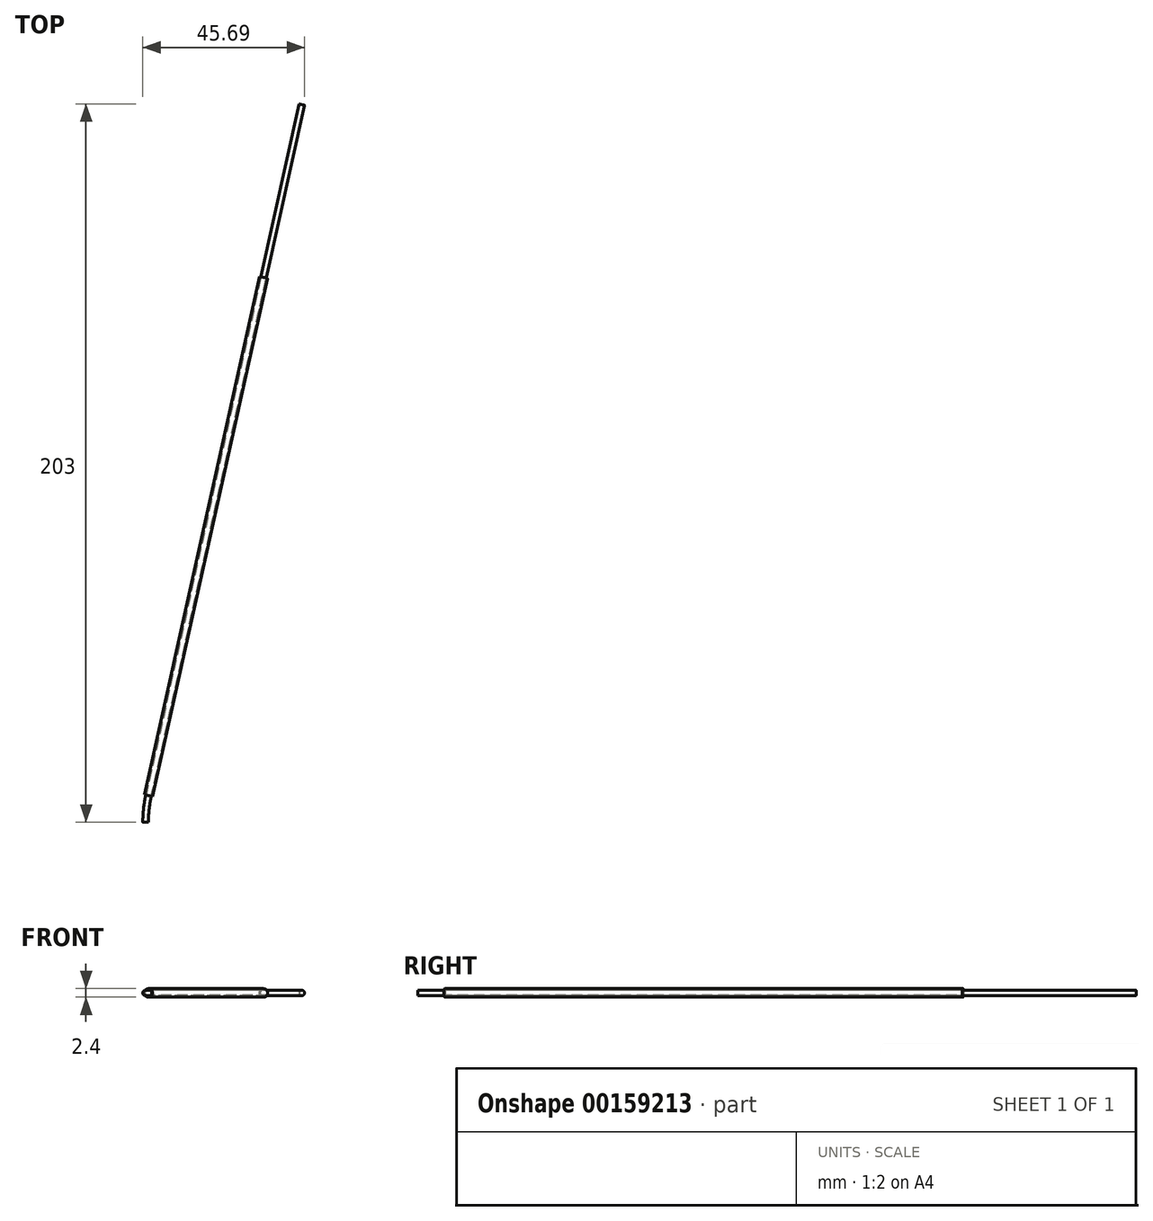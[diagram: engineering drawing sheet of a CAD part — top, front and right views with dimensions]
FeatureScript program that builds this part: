
annotation { "Feature Type Name" : "Feature", "Feature Type Description" : "" }
export const myFeature = defineFeature(function(context is Context, id is Id, definition is map)
    precondition{}
    {
        {
            assignVariable(context, id + "F0", {"name" : "TubeTransmissionLength", "anyValue" : 200});
        }
        {
            assignVariable(context, id + "F1", {"name" : "Angle", "anyValue" : 12.5});
        }
        {
            var Q0;
            Q0=qCreatedBy(makeId("Front.planeOp"),FACE);
            var sketch = newSketch(context, id + "F2", { "sketchPlane" : qUnion([Q0])});
            skCircle(sketch, "E0", {"center": v(0, 0) * mm, "radius": 0.7 * mm});
            skCircle(sketch, "E1", {"center": v(0, 0) * mm, "radius": 0.8 * mm});
            skSolve(sketch);
        }
        {
            var Q0;
            Q0=qCreatedBy(makeId("Top.planeOp"),FACE);
            var sketch = newSketch(context, id + "F3", { "sketchPlane" : qUnion([Q0])});
            skLineSegment(sketch, "E2", {"start": v(0, 0) * mm, "end": v(0, -200) * mm});
            skLineSegment(sketch, "E3", {"start": v(0, -145.32) * mm, "end": v(0, -200) * mm, "construction": true});
            skLineSegment(sketch, "E4", {"start": v(0, -200) * mm, "end": v(-35, -200) * mm, "construction": true});
            skArc(sketch, "E5", {"start": v(0, -200) * mm, "mid": v(-0.2, -203.8) * mm, "end": v(-0.83, -207.57) * mm});
            skSolve(sketch);
        }
        {
            var Q0;
            Q0=makeQuery(id+"F2.imprint","IMPRINT",FACE,{"disambiguationData":[TD([[makeQuery(id+"F2.imprint","IMPRINT",EDGE,{"derivedFrom":sQuery(id+"F2.wireOp",EDGE,"E0")}),-1.0]])]});
            var Q1;
            Q1=sQuery(id+"F3.wireOp",EDGE,"E2");
            var Q2;
            Q2=sQuery(id+"F3.wireOp",EDGE,"E5");
            sweep(context, id + "F4", {"profiles" : qUnion([Q0]), "path" : qUnion([Q1, Q2])});
        }
        {
            var Q0;
            Q0=makeQuery(id+"F4.opSweep","CAP_FACE",FACE,{"disambiguationData":[OSD([sQuery(id+"F2.wireOp",EDGE,"E0"),sQuery(id+"F2.wireOp",EDGE,"E1"),sQuery(id+"F3.wireOp",VERTEX,"E2.start")])],"isStart":true});
            cPlane(context, id + "F5", {"entities" : qUnion([Q0]), "cplaneType" : CPlaneType.OFFSET, "offset" : 50 * mm, "oppositeDirection" : true, "width" : 150 * mm, "height" : 150 * mm});
        }
        {
            var Q0;
            Q0=qCreatedBy(id+"F5.planeOp",FACE);
            var sketch = newSketch(context, id + "F6", { "sketchPlane" : qUnion([Q0])});
            skCircle(sketch, "E6.0", {"center": v(0, 0) * mm, "radius": 0.8 * mm});
            skCircle(sketch, "E6.1", {"center": v(0, 0) * mm, "radius": 0.7 * mm});
            skCircle(sketch, "E7", {"center": v(0, 0) * mm, "radius": 0.9 * mm});
            skCircle(sketch, "E8", {"center": v(0, 0) * mm, "radius": 1.2 * mm});
            skSolve(sketch);
        }
        {
            var Q0;
            Q0=makeQuery(id+"F6.imprint","IMPRINT",FACE,{"disambiguationData":[TD([[makeQuery(id+"F6.imprint","IMPRINT",EDGE,{"derivedFrom":sQuery(id+"F6.wireOp",EDGE,"E7")}),-1.0]])]});
            var Q1;
            Q1=makeQuery(id+"F4.opSweep","SWEPT_FACE",FACE,{"disambiguationData":[OSD([sQuery(id+"F2.wireOp",EDGE,"E1"),sQuery(id+"F3.wireOp",EDGE,"E2")])]});
            extrude(context, id + "F7", {"entities" : qUnion([Q0]), "oppositeDirection" : true, "endBoundEntityFace" : qUnion([Q1]), "depth" : (getVariable(context, 'TubeTransmissionLength') - 50) * mm});
        }
        {
            var Q0;
            Q0=makeQuery(id+"F7.opExtrude","CAP_FACE",FACE,{"disambiguationData":[OSD([sQuery(id+"F6.wireOp",EDGE,"E7"),sQuery(id+"F6.wireOp",EDGE,"E8")])],"isStart":true});
            cPlane(context, id + "F8", {"entities" : qUnion([Q0]), "cplaneType" : CPlaneType.OFFSET, "offset" : 50 * mm, "oppositeDirection" : true, "width" : 150 * mm, "height" : 150 * mm});
        }
        {
            var Q0;
            Q0=qCreatedBy(id+"F8.planeOp",FACE);
            var sketch = newSketch(context, id + "F9", { "sketchPlane" : qUnion([Q0])});
            skCircle(sketch, "E9.0", {"center": v(0, 0) * mm, "radius": 1.2 * mm});
            skLineSegment(sketch, "E10", {"start": v(0, 0) * mm, "end": v(0, 9.07) * mm});
            skLineSegment(sketch, "E11", {"start": v(0, 0) * mm, "end": v(-8.67, 0) * mm});
            skSolve(sketch);
        }
        {
            var Q0;
            Q0=makeQuery(id+"F7.opExtrude","SWEPT_BODY",BODY,{"disambiguationData":[OSD([sQuery(id+"F6.wireOp",EDGE,"E7"),sQuery(id+"F6.wireOp",EDGE,"E8")])]});
            var Q1;
            Q1=makeQuery(id+"F4.opSweep","SWEPT_BODY",BODY,{"disambiguationData":[OSD([sQuery(id+"F2.wireOp",EDGE,"E0"),sQuery(id+"F2.wireOp",EDGE,"E1"),sQuery(id+"F3.wireOp",EDGE,"E5")])]});
            transform(context, id + "F10", {"entities" : qUnion([Q0, Q1]), "transformType" : TransformType.TRANSLATION_3D, "dx" : 0 * mm, "dy" : 4.7 * mm, "dz" : 0 * mm, "makeCopy" : false});
        }
        {
            var Q0;
            Q0=makeQuery(id+"F7.opExtrude","SWEPT_BODY",BODY,{"disambiguationData":[OSD([sQuery(id+"F6.wireOp",EDGE,"E7"),sQuery(id+"F6.wireOp",EDGE,"E8")])]});
            var Q1;
            Q1=makeQuery(id+"F4.opSweep","SWEPT_BODY",BODY,{"disambiguationData":[OSD([sQuery(id+"F2.wireOp",EDGE,"E0"),sQuery(id+"F2.wireOp",EDGE,"E1"),sQuery(id+"F3.wireOp",EDGE,"E5")])]});
            var Q2;
            Q2=sQuery(id+"F9.wireOp",EDGE,"E10");
            transform(context, id + "F11", {"entities" : qUnion([Q0, Q1]), "transformType" : TransformType.ROTATION, "transformAxis" : qUnion([Q2]), "angle" : (getVariable(context, 'Angle')) * degree, "makeCopy" : false});
        }
        {
            var Q0;
            Q0=makeQuery(id+"F7.opExtrude","SWEPT_BODY",BODY,{"disambiguationData":[OSD([sQuery(id+"F6.wireOp",EDGE,"E7"),sQuery(id+"F6.wireOp",EDGE,"E8")])]});
            var Q1;
            Q1=makeQuery(id+"F4.opSweep","SWEPT_BODY",BODY,{"disambiguationData":[OSD([sQuery(id+"F2.wireOp",EDGE,"E0"),sQuery(id+"F2.wireOp",EDGE,"E1"),sQuery(id+"F3.wireOp",EDGE,"E5")])]});
            var Q2;
            Q2=sQuery(id+"F3.wireOp",EDGE,"E2");
            transform(context, id + "F12", {"entities" : qUnion([Q0, Q1]), "transformType" : TransformType.ROTATION, "transformAxis" : qUnion([Q2]), "angle" : 180 * degree, "makeCopy" : false});
        }
    });
